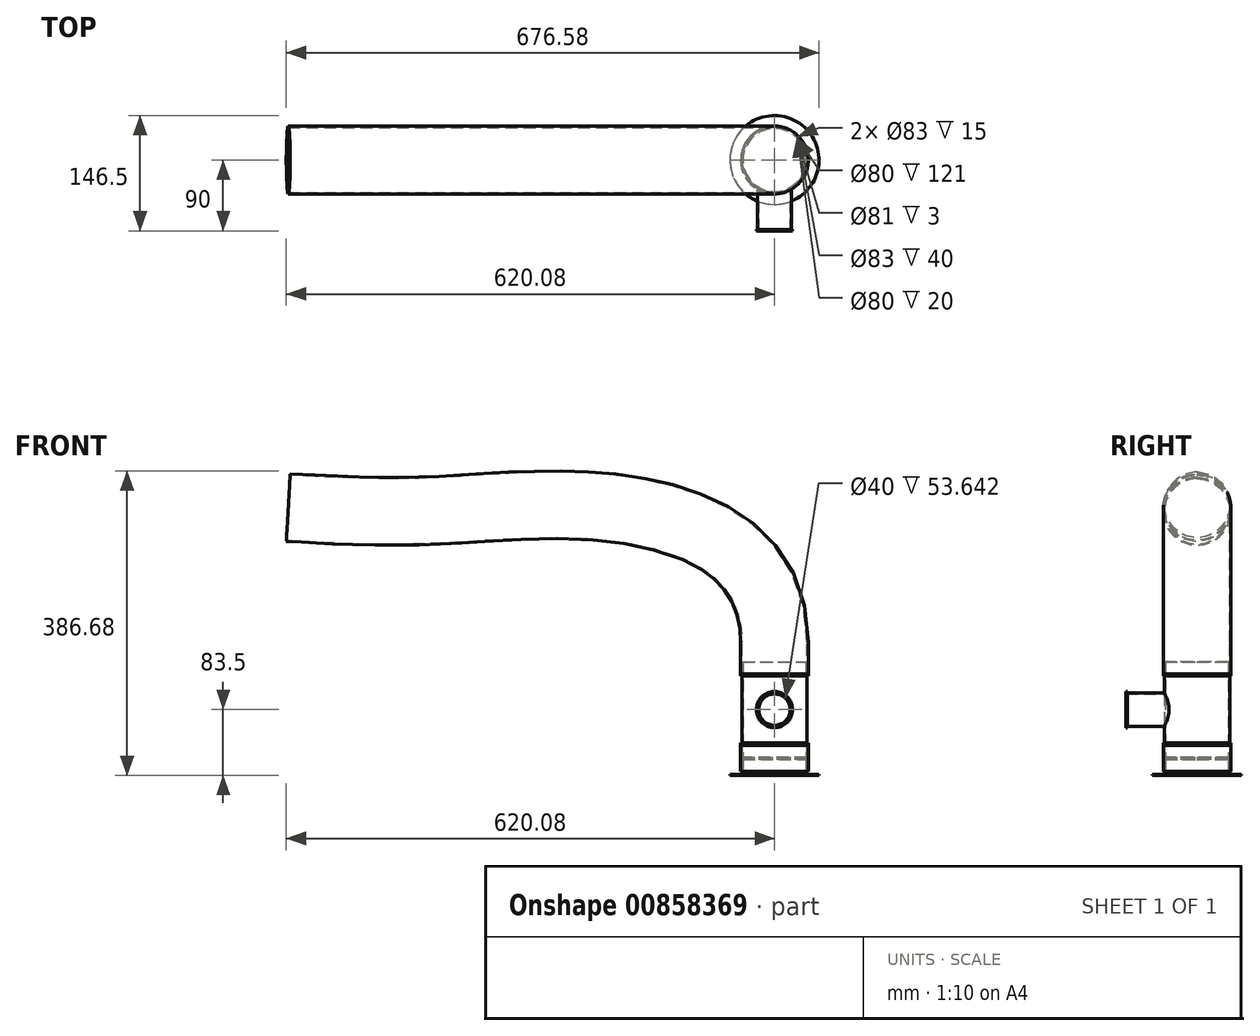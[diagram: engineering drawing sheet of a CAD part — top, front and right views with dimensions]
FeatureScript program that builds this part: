
annotation { "Feature Type Name" : "Feature", "Feature Type Description" : "" }
export const myFeature = defineFeature(function(context is Context, id is Id, definition is map)
    precondition{}
    {
        {
            var Q0;
            Q0=qCreatedBy(makeId("Front.planeOp"),FACE);
            var sketch = newSketch(context, id + "F0", { "sketchPlane" : qUnion([Q0])});
            skLineSegment(sketch, "E0", {"start": v(56.5, 0) * mm, "end": v(56.5, 1.5) * mm});
            skLineSegment(sketch, "E1", {"start": v(56.5, 1.5) * mm, "end": v(41.5, 1.5) * mm});
            skLineSegment(sketch, "E2", {"start": v(41.5, 1.5) * mm, "end": v(41.5, 20) * mm});
            skLineSegment(sketch, "E3", {"start": v(41.5, 20) * mm, "end": v(40, 20) * mm});
            skLineSegment(sketch, "E4", {"start": v(40, 20) * mm, "end": v(40, 0) * mm});
            skLineSegment(sketch, "E5", {"start": v(56.5, 0) * mm, "end": v(40, 0) * mm});
            skLineSegment(sketch, "E6", {"start": v(0, 0) * mm, "end": v(0, 20) * mm, "construction": true});
            skSolve(sketch);
        }
        {
            var Q0;
            Q0=makeQuery(id+"F0.imprint","IMPRINT",FACE,{"disambiguationData":[TD([[makeQuery(id+"F0.imprint","IMPRINT",EDGE,{"derivedFrom":sQuery(id+"F0.wireOp",EDGE,"E0")}),1.0]])]});
            var Q1;
            Q1=sQuery(id+"F0.wireOp",EDGE,"E6");
            revolve(context, id + "F1", {"surfaceOperationType" : NewSurfaceOperationType.NEW, "entities" : qUnion([Q0]), "axis" : qUnion([Q1]), "revolveType" : RevolveType.FULL});
        }
        {
            var Q0;
            Q0=qCreatedBy(makeId("Front.planeOp"),FACE);
            var sketch = newSketch(context, id + "F2", { "sketchPlane" : qUnion([Q0])});
            skLineSegment(sketch, "E7", {"start": v(41.5, 5) * mm, "end": v(41.5, 20) * mm});
            skLineSegment(sketch, "E8", {"start": v(41.5, 5) * mm, "end": v(43, 5) * mm});
            skLineSegment(sketch, "E9", {"start": v(43, 5) * mm, "end": v(43, 38) * mm});
            skLineSegment(sketch, "E10", {"start": v(43, 38) * mm, "end": v(41.5, 38) * mm});
            skLineSegment(sketch, "E11", {"start": v(41.5, 38) * mm, "end": v(41.5, 23) * mm});
            skLineSegment(sketch, "E12", {"start": v(41.5, 20) * mm, "end": v(40.5, 20) * mm});
            skLineSegment(sketch, "E13", {"start": v(40.5, 20) * mm, "end": v(40.5, 23) * mm});
            skLineSegment(sketch, "E14", {"start": v(40.5, 23) * mm, "end": v(41.5, 23) * mm});
            skLineSegment(sketch, "E15", {"start": v(0, 38) * mm, "end": v(0, 5) * mm});
            skSolve(sketch);
        }
        {
            var Q0;
            Q0 = qSketchRegion(id + "F2", true);
            var Q1;
            Q1=sQuery(id+"F2.wireOp",EDGE,"E15");
            revolve(context, id + "F3", {"surfaceOperationType" : NewSurfaceOperationType.NEW, "entities" : qUnion([Q0]), "axis" : qUnion([Q1]), "revolveType" : RevolveType.FULL});
        }
        {
            var Q0;
            Q0=qCreatedBy(makeId("Front.planeOp"),FACE);
            var sketch = newSketch(context, id + "F4", { "sketchPlane" : qUnion([Q0])});
            skLineSegment(sketch, "E16", {"start": v(-41.5, 23) * mm, "end": v(-41.5, 38) * mm});
            skLineSegment(sketch, "E17", {"start": v(-41.5, 38) * mm, "end": v(-43, 38) * mm});
            skLineSegment(sketch, "E18", {"start": v(-43, 129) * mm, "end": v(-41.5, 129) * mm});
            skLineSegment(sketch, "E19", {"start": v(-41.5, 129) * mm, "end": v(-41.5, 144) * mm});
            skLineSegment(sketch, "E20", {"start": v(-41.5, 144) * mm, "end": v(-40, 144) * mm});
            skLineSegment(sketch, "E21", {"start": v(-40, 144) * mm, "end": v(-40, 23) * mm});
            skLineSegment(sketch, "E22", {"start": v(-40, 23) * mm, "end": v(-41.5, 23) * mm});
            skLineSegment(sketch, "E23", {"start": v(0, 23) * mm, "end": v(0, 144) * mm, "construction": true});
            skLineSegment(sketch, "E24", {"start": v(-43, 41) * mm, "end": v(-41.5, 41) * mm});
            skLineSegment(sketch, "E25", {"start": v(-41.5, 41) * mm, "end": v(-41.5, 126) * mm});
            skLineSegment(sketch, "E26", {"start": v(-41.5, 126) * mm, "end": v(-43, 126) * mm});
            skLineSegment(sketch, "E27", {"start": v(-43, 126) * mm, "end": v(-43, 129) * mm});
            skLineSegment(sketch, "E28", {"start": v(-43, 41) * mm, "end": v(-43, 38) * mm});
            skSolve(sketch);
        }
        {
            var Q0;
            Q0=makeQuery(id+"F4.imprint","IMPRINT",FACE,{"disambiguationData":[TD([[makeQuery(id+"F4.imprint","IMPRINT",EDGE,{"derivedFrom":sQuery(id+"F4.wireOp",EDGE,"E16")}),-1.0]])]});
            var Q1;
            Q1=sQuery(id+"F4.wireOp",EDGE,"E23");
            revolve(context, id + "F5", {"surfaceOperationType" : NewSurfaceOperationType.NEW, "entities" : qUnion([Q0]), "axis" : qUnion([Q1]), "revolveType" : RevolveType.FULL});
        }
        {
            var Q0;
            Q0=qCreatedBy(makeId("Right.planeOp"),FACE);
            var sketch = newSketch(context, id + "F6", { "sketchPlane" : qUnion([Q0])});
            skLineSegment(sketch, "E29", {"start": v(-45, 83.5) * mm, "end": v(-90, 83.5) * mm, "construction": true});
            skLineSegment(sketch, "E30", {"start": v(-45, 105) * mm, "end": v(-88.5, 105) * mm});
            skLineSegment(sketch, "E31", {"start": v(-88.5, 105) * mm, "end": v(-88.5, 106.5) * mm});
            skLineSegment(sketch, "E32", {"start": v(-88.5, 106.5) * mm, "end": v(-90, 106.5) * mm});
            skLineSegment(sketch, "E33", {"start": v(-90, 106.5) * mm, "end": v(-90, 103.5) * mm});
            skLineSegment(sketch, "E34", {"start": v(-90, 103.5) * mm, "end": v(-45, 103.5) * mm});
            skLineSegment(sketch, "E35", {"start": v(-45, 103.5) * mm, "end": v(-45, 105) * mm});
            skSolve(sketch);
        }
        {
            var Q0;
            Q0=makeQuery(id+"F6.imprint","IMPRINT",FACE,{"disambiguationData":[TD([[makeQuery(id+"F6.imprint","IMPRINT",EDGE,{"derivedFrom":sQuery(id+"F6.wireOp",EDGE,"E30")}),1.0]])]});
            var Q1;
            Q1=sQuery(id+"F6.wireOp",EDGE,"E29");
            revolve(context, id + "F7", {"operationType" : NewBodyOperationType.ADD, "surfaceOperationType" : NewSurfaceOperationType.NEW, "entities" : qUnion([Q0]), "axis" : qUnion([Q1]), "revolveType" : RevolveType.FULL});
        }
        {
            var Q0;
            Q0=makeQuery(id+"F7.opRevolve","SWEPT_FACE",FACE,{"disambiguationData":[OSD([sQuery(id+"F6.wireOp",EDGE,"E35")])]});
            extrude(context, id + "F8", {"entities" : qUnion([Q0]), "operationType" : NewBodyOperationType.ADD, "endBound" : BoundingType.UP_TO_NEXT, "depth" : 25 * mm, "offsetDistance" : 25 * mm});
        }
        {
            var Q0;
            Q0=makeQuery(id+"F5.opRevolve","SWEPT_FACE",FACE,{"disambiguationData":[OSD([sQuery(id+"F4.wireOp",EDGE,"E18")])]});
            cPlane(context, id + "F9", {"entities" : qUnion([Q0]), "cplaneType" : CPlaneType.OFFSET, "offset" : 0 * mm, "width" : 150 * mm, "height" : 150 * mm});
        }
        {
            var Q0;
            Q0=qCreatedBy(makeId("Front.planeOp"),FACE);
            var sketch = newSketch(context, id + "F10", { "sketchPlane" : qUnion([Q0])});
            skLineSegment(sketch, "E36", {"start": v(0, 169) * mm, "end": v(0, 129) * mm});
            skFitSpline(sketch, "E37", {"points": [v(0, 169) * mm, v(-165.05, 333.5) * mm, v(-420.45, 337.13) * mm, v(-617.6, 340.2) * mm], "startDerivative": vector(0, 926.72) * mm, "endDerivative": vector(-761.89, 43.88) * mm});
            skSolve(sketch);
        }
        {
            var Q0;
            Q0=qCreatedBy(id+"F9.planeOp",FACE);
            var sketch = newSketch(context, id + "F11", { "sketchPlane" : qUnion([Q0])});
            skCircle(sketch, "E38", {"center": v(0, 0) * mm, "radius": 43 * mm});
            skCircle(sketch, "E39", {"center": v(0, 0) * mm, "radius": 41.5 * mm});
            skSolve(sketch);
        }
        {
            var Q0;
            Q0 = qSketchRegion(id + "F11", true);
            var Q1;
            Q1=sQuery(id+"F10.wireOp",EDGE,"E36");
            var Q2;
            Q2=sQuery(id+"F10.wireOp",EDGE,"E37");
            sweep(context, id + "F12", {"profiles" : qUnion([Q0]), "path" : qUnion([Q1, Q2])});
        }
    });
